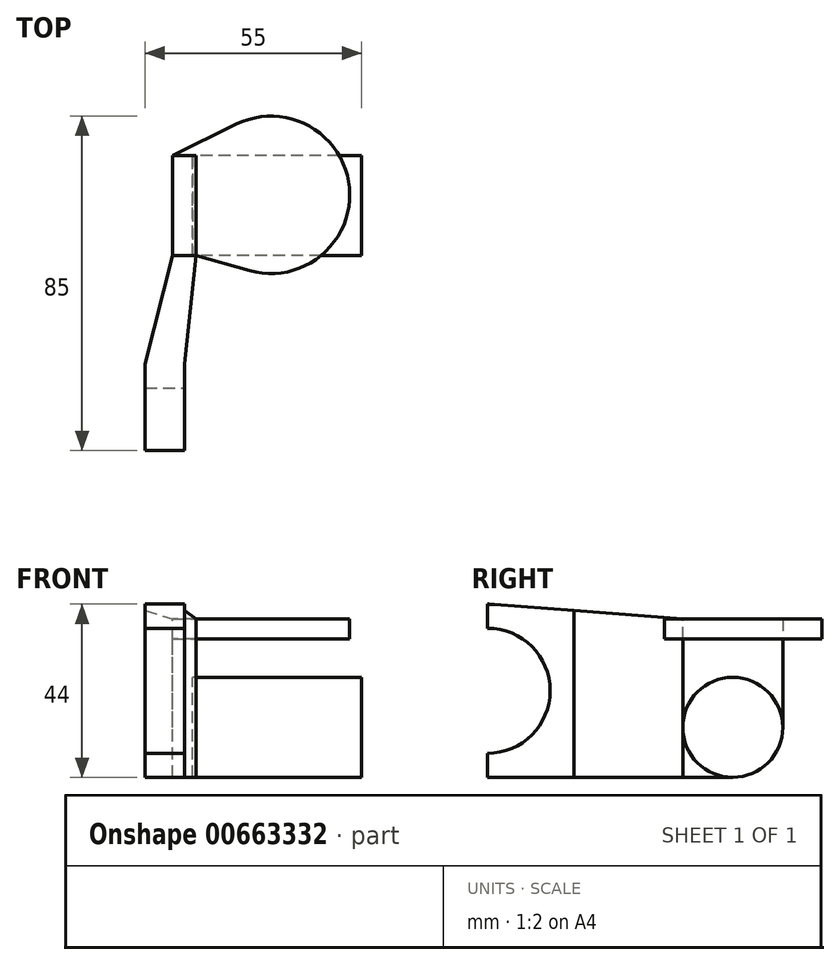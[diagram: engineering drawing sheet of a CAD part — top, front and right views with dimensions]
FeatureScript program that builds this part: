
annotation { "Feature Type Name" : "Feature", "Feature Type Description" : "" }
export const myFeature = defineFeature(function(context is Context, id is Id, definition is map)
    precondition{}
    {
        {
            var Q0;
            Q0=qCreatedBy(makeId("Right.planeOp"),FACE);
            var sketch = newSketch(context, id + "F0", { "sketchPlane" : qUnion([Q0])});
            skLineSegment(sketch, "E0", {"start": v(0, 0) * mm, "end": v(0, 0) * mm});
            skLineSegment(sketch, "E1", {"start": v(0, 0) * mm, "end": v(-22, 0) * mm});
            skPoint(sketch, "E2", {"position": v(-15.9, 0) * mm});
            skPoint(sketch, "E3", {"position": v(-22, 0) * mm});
            skLineSegment(sketch, "E4", {"start": v(0, 0) * mm, "end": v(0, 15.7) * mm, "construction": true});
            skCircle(sketch, "E5.converted", {"center": v(0, 0) * mm, "radius": 15.9 * mm});
            skCircle(sketch, "E6.converted", {"center": v(0, 0) * mm, "radius": 22 * mm});
            skLineSegment(sketch, "E7", {"start": v(0, 15.7) * mm, "end": v(0, 22) * mm});
            skLineSegment(sketch, "E8", {"start": v(0, 0) * mm, "end": v(0, -22) * mm});
            skLineSegment(sketch, "E9", {"start": v(0, -22) * mm, "end": v(62.3, -22) * mm});
            skLineSegment(sketch, "E10", {"start": v(62.3, -22) * mm, "end": v(62.3, -9.3) * mm, "construction": true});
            skLineSegment(sketch, "E11", {"start": v(0, 0) * mm, "end": v(75, 0) * mm, "construction": true});
            skLineSegment(sketch, "E12", {"start": v(62.3, -9.3) * mm, "end": v(75, -9.3) * mm, "construction": true});
            skLineSegment(sketch, "E13", {"start": v(75, -9.3) * mm, "end": v(75, 0) * mm});
            skCircle(sketch, "E14", {"center": v(62.3, -9.3) * mm, "radius": 12.7 * mm});
            skLineSegment(sketch, "E15", {"start": v(75, 0) * mm, "end": v(75, 18.2) * mm});
            skLineSegment(sketch, "E16", {"start": v(49.6, 18.2) * mm, "end": v(1.7, 21.93) * mm});
            skLineSegment(sketch, "E17", {"start": v(22, 0) * mm, "end": v(22, 20.35) * mm});
            skLineSegment(sketch, "E18", {"start": v(22, 0) * mm, "end": v(22, -22) * mm});
            skLineSegment(sketch, "E19", {"start": v(49.6, -22) * mm, "end": v(49.6, 18.2) * mm});
            skPoint(sketch, "E20.orphan", {"position": v(49.6, -9.3) * mm});
            skLineSegment(sketch, "E21", {"start": v(49.6, 18.2) * mm, "end": v(75, 18.2) * mm});
            skLineSegment(sketch, "E22", {"start": v(49.6, 13.2) * mm, "end": v(65, 13.2) * mm});
            skCircle(sketch, "E23", {"center": v(35.07, -14.5) * mm, "radius": 7.5 * mm, "construction": true});
            skCircle(sketch, "E24", {"center": v(35.07, -14.5) * mm, "radius": 2.5 * mm});
            skLineSegment(sketch, "E25", {"start": v(35.07, -14.5) * mm, "end": v(35.07, -22) * mm, "construction": true});
            skSolve(sketch);
        }
        {
            var Q0;
            {var subQ3=sQuery(id+"F0.wireOp",EDGE,"EyoTU6OX-oxVw-CAXq-iYRt-Jc2Cb9K9qKyU");Q0=makeQuery(id+"F0.imprint","IMPRINT",FACE,{"disambiguationData":[TD([[makeQuery(id+"F0.imprint","IMPRINT",EDGE,{"derivedFrom":subQ3}),1.0]])]});}
            var Q1;
            {var subQ0=sQuery(id+"F0.wireOp",EDGE,"vLBDvG5Z-B58P-mFEn-qBut-4CCsbW0nsGNk");Q1=makeQuery(id+"F0.imprint","IMPRINT",FACE,{"disambiguationData":[TD([[makeQuery(id+"F0.imprint","IMPRINT",EDGE,{"derivedFrom":subQ0}),-1.0]])]});}
            var Q2;
            {var subQ2=sQuery(id+"F0.wireOp",EDGE,"vsm7txV6-gibO-x3vs-kBa2-syee0zq67u89");var subQ5=sQuery(id+"F0.wireOp",EDGE,"E5.converted");var subQ7=makeQuery(id+"F0.imprint","INTERSECT",VERTEX,{"derivedFrom":[subQ2,subQ5]});Q2=makeQuery(id+"F0.imprint","IMPRINT",FACE,{"disambiguationData":[TD([[makeQuery(id+"F0.imprint","IMPRINT",EDGE,{"disambiguationData":[TD([[subQ7,-1.0]])],"derivedFrom":subQ2}),1.0]])]});}
            var Q3;
            {var subQ0=sQuery(id+"F0.wireOp",EDGE,"E7");var subQ7=sQuery(id+"F0.wireOp",EDGE,"E5.converted");var subQ8=makeQuery(id+"F0.imprint","INTERSECT",VERTEX,{"derivedFrom":[subQ7,subQ0]});Q3=makeQuery(id+"F0.imprint","IMPRINT",FACE,{"disambiguationData":[TD([[makeQuery(id+"F0.imprint","IMPRINT",EDGE,{"disambiguationData":[TD([[subQ8,1.0]])],"derivedFrom":subQ7}),-1.0]])]});}
            var Q4;
            {var subQ3=sQuery(id+"F0.wireOp",EDGE,"E17");Q4=makeQuery(id+"F0.imprint","IMPRINT",FACE,{"disambiguationData":[TD([[makeQuery(id+"F0.imprint","IMPRINT",EDGE,{"derivedFrom":subQ3}),1.0]])]});}
            var Q5;
            {var subQ3=sQuery(id+"F0.wireOp",EDGE,"E18");Q5=makeQuery(id+"F0.imprint","IMPRINT",FACE,{"disambiguationData":[TD([[makeQuery(id+"F0.imprint","IMPRINT",EDGE,{"derivedFrom":subQ3}),-1.0]])]});}
            extrude(context, id + "F1", {"entities" : qUnion([Q0, Q1, Q2, Q3, Q4, Q5]), "oppositeDirection" : true, "depth" : 10 * mm, "offsetDistance" : 25 * mm});
        }
        {
            var Q0;
            {var subQ0=sQuery(id+"F0.wireOp",EDGE,"JMXsvigg-hWFq-6zV7-Z0Ly-zUxmX8QfqniT");var subQ1=sQuery(id+"F0.wireOp",EDGE,"rdb2OAyp-sVdK-5mbn-yiX8-J6zx6s2CCEKt");var subQ2=makeQuery(id+"F0.imprint","INTERSECT",VERTEX,{"derivedFrom":[subQ1,subQ0]});Q0=makeQuery(id+"F0.imprint","IMPRINT",FACE,{"disambiguationData":[TD([[makeQuery(id+"F0.imprint","IMPRINT",EDGE,{"disambiguationData":[TD([[subQ2,-1.0]])],"derivedFrom":subQ1}),-1.0]])]});}
            var Q1;
            {var subQ0=sQuery(id+"F0.wireOp",EDGE,"rdb2OAyp-sVdK-5mbn-yiX8-J6zx6s2CCEKt");var subQ1=sQuery(id+"F0.wireOp",EDGE,"gJmcAM5a-D3O1-cz5J-tmTC-PMyA3bws1ZkG");var subQ2=makeQuery(id+"F0.imprint","INTERSECT",VERTEX,{"derivedFrom":[subQ1,subQ0]});Q1=makeQuery(id+"F0.imprint","IMPRINT",FACE,{"disambiguationData":[TD([[makeQuery(id+"F0.imprint","IMPRINT",EDGE,{"disambiguationData":[TD([[subQ2,1.0]])],"derivedFrom":subQ0}),-1.0]])]});}
            var Q2;
            {var subQ0=sQuery(id+"F0.wireOp",EDGE,"gJmcAM5a-D3O1-cz5J-tmTC-PMyA3bws1ZkG");var subQ3=makeQuery(id+"F0.imprint","INTERSECT",VERTEX,{"derivedFrom":[subQ0,sQuery(id+"F0.wireOp",EDGE,"mCT7uVDd-ZWGn-XHnn-A05l-v2yQsC5TML3c")]});Q2=makeQuery(id+"F0.imprint","IMPRINT",FACE,{"disambiguationData":[TD([[makeQuery(id+"F0.imprint","IMPRINT",EDGE,{"disambiguationData":[TD([[subQ3,1.0]])],"derivedFrom":subQ0}),1.0]])]});}
            var Q3;
            {var subQ0=sQuery(id+"F0.wireOp",EDGE,"ZvWxcYq7-Yi8d-8ZP1-fmEg-x5NWmN5w42XX");Q3=makeQuery(id+"F0.imprint","IMPRINT",FACE,{"disambiguationData":[TD([[makeQuery(id+"F0.imprint","IMPRINT",EDGE,{"derivedFrom":subQ0}),1.0]])]});}
            var Q4;
            {var subQ0=sQuery(id+"F0.wireOp",EDGE,"ZvWxcYq7-Yi8d-8ZP1-fmEg-x5NWmN5w42XX");Q4=makeQuery(id+"F0.imprint","IMPRINT",FACE,{"disambiguationData":[TD([[makeQuery(id+"F0.imprint","IMPRINT",EDGE,{"derivedFrom":subQ0}),-1.0]])]});}
            var Q5;
            {var subQ1=sQuery(id+"F0.wireOp",EDGE,"E13");Q5=makeQuery(id+"F0.imprint","IMPRINT",FACE,{"disambiguationData":[TD([[makeQuery(id+"F0.imprint","IMPRINT",EDGE,{"derivedFrom":subQ1}),1.0]])]});}
            var Q6;
            {var subQ0=sQuery(id+"F0.wireOp",EDGE,"E14");var subQ1=makeQuery(id+"F0.imprint","INTERSECT",VERTEX,{"derivedFrom":[sQuery(id+"F0.wireOp",EDGE,"E13"),subQ0]});Q6=makeQuery(id+"F0.imprint","IMPRINT",FACE,{"disambiguationData":[TD([[makeQuery(id+"F0.imprint","IMPRINT",EDGE,{"disambiguationData":[TD([[subQ1,-1.0]])],"derivedFrom":subQ0}),1.0]])]});}
            var Q7;
            {var subQ0=sQuery(id+"F0.wireOp",EDGE,"E14");var subQ1=sQuery(id+"F0.wireOp",EDGE,"E9");var subQ2=makeQuery(id+"F0.imprint","INTERSECT",VERTEX,{"derivedFrom":[subQ1,subQ0]});Q7=makeQuery(id+"F0.imprint","IMPRINT",FACE,{"disambiguationData":[TD([[makeQuery(id+"F0.imprint","IMPRINT",EDGE,{"disambiguationData":[TD([[subQ2,1.0]])],"derivedFrom":subQ1}),1.0]])]});}
            var Q8;
            {var subQ0=sQuery(id+"F0.wireOp",EDGE,"E21");Q8=makeQuery(id+"F0.imprint","IMPRINT",FACE,{"disambiguationData":[TD([[makeQuery(id+"F0.imprint","IMPRINT",EDGE,{"derivedFrom":subQ0}),-1.0]])]});}
            extrude(context, id + "F2", {"entities" : qUnion([Q0, Q1, Q2, Q3, Q4, Q5, Q6, Q7, Q8]), "depth" : 3 * mm, "offsetDistance" : 25 * mm, "hasSecondDirection" : true, "secondDirectionOppositeDirection" : true, "secondDirectionDepth" : 3 * mm});
        }
        {
            var Q0;
            Q0=makeQuery(id+"F1.opExtrude","SWEPT_FACE",FACE,{"disambiguationData":[OSD([sQuery(id+"F0.wireOp",EDGE,"E17"),sQuery(id+"F0.wireOp",EDGE,"E18")])]});
            var Q1;
            Q1=makeQuery(id+"F2.opExtrude","SWEPT_FACE",FACE,{"disambiguationData":[OSD([sQuery(id+"F0.wireOp",EDGE,"E19")])]});
            loft(context, id + "F3", {"sheetProfilesArray" : [{ "sheetProfileEntities" : qUnion([Q0]) }, { "sheetProfileEntities" : qUnion([Q1]) }]});
        }
        {
            var Q0;
            Q0=makeQuery(id+"F1.opExtrude","SWEPT_BODY",BODY,{"disambiguationData":[OSD([sQuery(id+"F0.wireOp",EDGE,"E1"),sQuery(id+"F0.wireOp",EDGE,"vsm7txV6-gibO-x3vs-kBa2-syee0zq67u89"),sQuery(id+"F0.wireOp",EDGE,"E5.converted"),sQuery(id+"F0.wireOp",EDGE,"E6.converted"),sQuery(id+"F0.wireOp",EDGE,"rdb2OAyp-sVdK-5mbn-yiX8-J6zx6s2CCEKt"),sQuery(id+"F0.wireOp",EDGE,"EyoTU6OX-oxVw-CAXq-iYRt-Jc2Cb9K9qKyU"),sQuery(id+"F0.wireOp",EDGE,"vLBDvG5Z-B58P-mFEn-qBut-4CCsbW0nsGNk")])]});
            var Q1;
            Q1=makeQuery(id+"F2.opExtrude","SWEPT_BODY",BODY,{"disambiguationData":[OSD([sQuery(id+"F0.wireOp",EDGE,"E9"),sQuery(id+"F0.wireOp",EDGE,"E13"),sQuery(id+"F0.wireOp",EDGE,"E14"),sQuery(id+"F0.wireOp",EDGE,"E15"),sQuery(id+"F0.wireOp",EDGE,"E19"),sQuery(id+"F0.wireOp",EDGE,"E21")])]});
            var Q2;
            Q2=makeQuery(id+"F3.opLoft","SWEPT_BODY",BODY,{"disambiguationData":[OSD([sQuery(id+"F0.wireOp",EDGE,"E17"),sQuery(id+"F0.wireOp",EDGE,"E18"),sQuery(id+"F0.wireOp",EDGE,"E19")])]});
            booleanBodies(context, id + "F4", {"operationType" : BooleanOperationType.UNION, "tools" : qUnion([Q0, Q1, Q2])});
        }
        {
            var Q0;
            Q0=makeQuery(id+"F2.opExtrude","SWEPT_FACE",FACE,{"disambiguationData":[OSD([sQuery(id+"F0.wireOp",EDGE,"E21")])]});
            extrude(context, id + "F5", {"entities" : qUnion([Q0]), "operationType" : NewBodyOperationType.REMOVE, "oppositeDirection" : true, "depth" : 5 * mm, "offsetDistance" : 25 * mm});
        }
        {
            var Q0;
            {var subQ0=sQuery(id+"F0.wireOp",EDGE,"E14");var subQ1=makeQuery(id+"F0.imprint","INTERSECT",VERTEX,{"derivedFrom":[sQuery(id+"F0.wireOp",EDGE,"E13"),subQ0]});Q0=makeQuery(id+"F0.imprint","IMPRINT",FACE,{"disambiguationData":[TD([[makeQuery(id+"F0.imprint","IMPRINT",EDGE,{"disambiguationData":[TD([[subQ1,-1.0]])],"derivedFrom":subQ0}),1.0]])]});}
            extrude(context, id + "F6", {"entities" : qUnion([Q0]), "depth" : 45 * mm, "offsetDistance" : 25 * mm, "hasSecondDirection" : true, "secondDirectionOppositeDirection" : false, "secondDirectionDepth" : 2 * mm});
        }
        {
            var Q0;
            Q0=makeQuery(id+"F5.boolean.opBoolean","COPY",FACE,{"derivedFrom":makeQuery(id+"F5.opExtrude","CAP_FACE",FACE,{"disambiguationData":[OSD([sQuery(id+"F0.wireOp",EDGE,"E21")])],"isStart":false})});
            var sketch = newSketch(context, id + "F7", { "sketchPlane" : qUnion([Q0])});
            skCircle(sketch, "E26", {"center": v(22, 65) * mm, "radius": 20 * mm});
            skLineSegment(sketch, "E27", {"start": v(-3, 49.6) * mm, "end": v(3, 49.6) * mm});
            skLineSegment(sketch, "E28", {"start": v(-3, 49.6) * mm, "end": v(-3, 75) * mm});
            skLineSegment(sketch, "E29", {"start": v(-3, 75) * mm, "end": v(13.18, 82.95) * mm});
            skLineSegment(sketch, "E30", {"start": v(3, 49.6) * mm, "end": v(16.54, 45.76) * mm});
            skSolve(sketch);
        }
        {
            var Q0;
            {var subQ0=sQuery(id+"F7.wireOp",EDGE,"E26");var subQ1=makeQuery(id+"F7.imprint","INTERSECT",VERTEX,{"derivedFrom":[subQ0,sQuery(id+"F7.wireOp",EDGE,"E29")]});Q0=makeQuery(id+"F7.imprint","IMPRINT",FACE,{"disambiguationData":[TD([[makeQuery(id+"F7.imprint","IMPRINT",EDGE,{"disambiguationData":[TD([[subQ1,1.0]])],"derivedFrom":subQ0}),1.0]])]});}
            var Q1;
            {var subQ0=sQuery(id+"F7.wireOp",EDGE,"E30");Q1=makeQuery(id+"F7.imprint","IMPRINT",FACE,{"disambiguationData":[TD([[makeQuery(id+"F7.imprint","IMPRINT",EDGE,{"derivedFrom":subQ0}),1.0]])]});}
            var Q2;
            {var subQ2=sQuery(id+"F7.wireOp",EDGE,"E27");Q2=makeQuery(id+"F7.imprint","IMPRINT",FACE,{"disambiguationData":[TD([[makeQuery(id+"F7.imprint","IMPRINT",EDGE,{"derivedFrom":subQ2}),-1.0]])]});}
            var Q3;
            {var subQ0=sQuery(id+"F7.wireOp",EDGE,"E29");Q3=makeQuery(id+"F7.imprint","IMPRINT",FACE,{"disambiguationData":[TD([[makeQuery(id+"F7.imprint","IMPRINT",EDGE,{"derivedFrom":subQ0}),-1.0]])]});}
            var Q4;
            {var subQ0=sQuery(id+"F7.wireOp",EDGE,"E26");var subQ1=sQuery(id+"F0.wireOp",EDGE,"E21");var subQ2=makeQuery(id+"F5.boolean.opBoolean","COPY",EDGE,{"derivedFrom":makeQuery(id+"F5.opExtrude","CAP_EDGE",EDGE,{"disambiguationData":[OSD([subQ1]),TDD([makeQuery(id+"F2.opExtrude","CAP_EDGE",EDGE,{"disambiguationData":[OSD([subQ1])],"isStart":false})])],"isStart":false})});var subQ3=makeQuery(id+"F7.imprint","INTERSECT",VERTEX,{"disambiguationData":[OD(0.0)],"derivedFrom":[subQ2,subQ0]});Q4=makeQuery(id+"F7.imprint","IMPRINT",FACE,{"disambiguationData":[TD([[makeQuery(id+"F7.imprint","IMPRINT",EDGE,{"disambiguationData":[TD([[subQ3,-1.0]])],"derivedFrom":subQ0}),1.0]])]});}
            extrude(context, id + "F8", {"entities" : qUnion([Q0, Q1, Q2, Q3, Q4]), "depth" : 5 * mm, "offsetDistance" : 25 * mm});
        }
    });
